# Revit family: Запорный клапан 4125 D
name_source: partatom
category: Rohrzubehör
revit_build: Autodesk Revit 2018 (Build: 20190510_1515(x64)
units: mm (PartAtom-declared; Revit-internal decimal feet)

## family parameters
Arbeitsebenenbasiert = Nein
Beim Laden mit Abzugskörper schneiden = Nein
Bemaßung runder Anschluss = Durchmesser verwenden
Gemeinsam genutzt = Nein
Immer vertikal = Ja
OmniClass-Nummer = 23.65.55.14
OmniClass-Titel = Valves for Liquid Services
Teiletyp = Unterbricht

## types (1)
- Запорный клапан 4125 D
    Hersteller = HERZ Armaturen Ges.m.b.H.
    L03 = 15 mm
    R03 = 9.5 mm  [stored 0.031168 ft]
    R100 = 1 mm  [stored 0.00328084 ft]
    S03 = 60 mm  [stored 0.19685 ft]
    SCRNCODE = 05;07;02
    SCRNSEQ = ARM;ARM_TYP="ABSV";2
    SW01 = 60.00°
    URL = www.herz-armaturen.ru
    W01 = 45.00°
    Букса = Латунь, устойчивая к селективной цинковой коррозии, CW602N
    Исполнение = STRÖMAX-D-запорный клапан с наклонным шпинделем, латунный корпус без покрытия, модель с длинными резьбовыми муфтами, неподнимающийся шпиндель, уплотнение шпинделя с помощью двойных уплотнительных колец O-Ring.
    Конус = Латунь, устойчивая к селективной цинковой коррозии, CW602N
    Корпус = Латунь, устойчивая к селективной цинковой коррозии, CC752S
    Макс. перепад давления на закрытом клапане = 1000000.0 Pa
    Макс. рабочая температура = 110 °C
    Макс. рабочее давление = 2000000.0 Pa
    Маховик = Пластик
    Область применения = Для перекрытия трубопроводов в системах отопления и холодоснабжения.
    Среда = Качество теплоносителя в соответствии с ÖNORM H5195 и/или предписаниями VDI 2035.
Разрешается использование смеси этилен- или пропиленгликоля в соотношении 25-50% с водой.
    Уплотнение = EPDM
    Шпиндель = Латунь CW617N

note: [stored X ft] marks values corroborated as IEEE doubles in the binary element streams (Revit-internal decimal feet)
